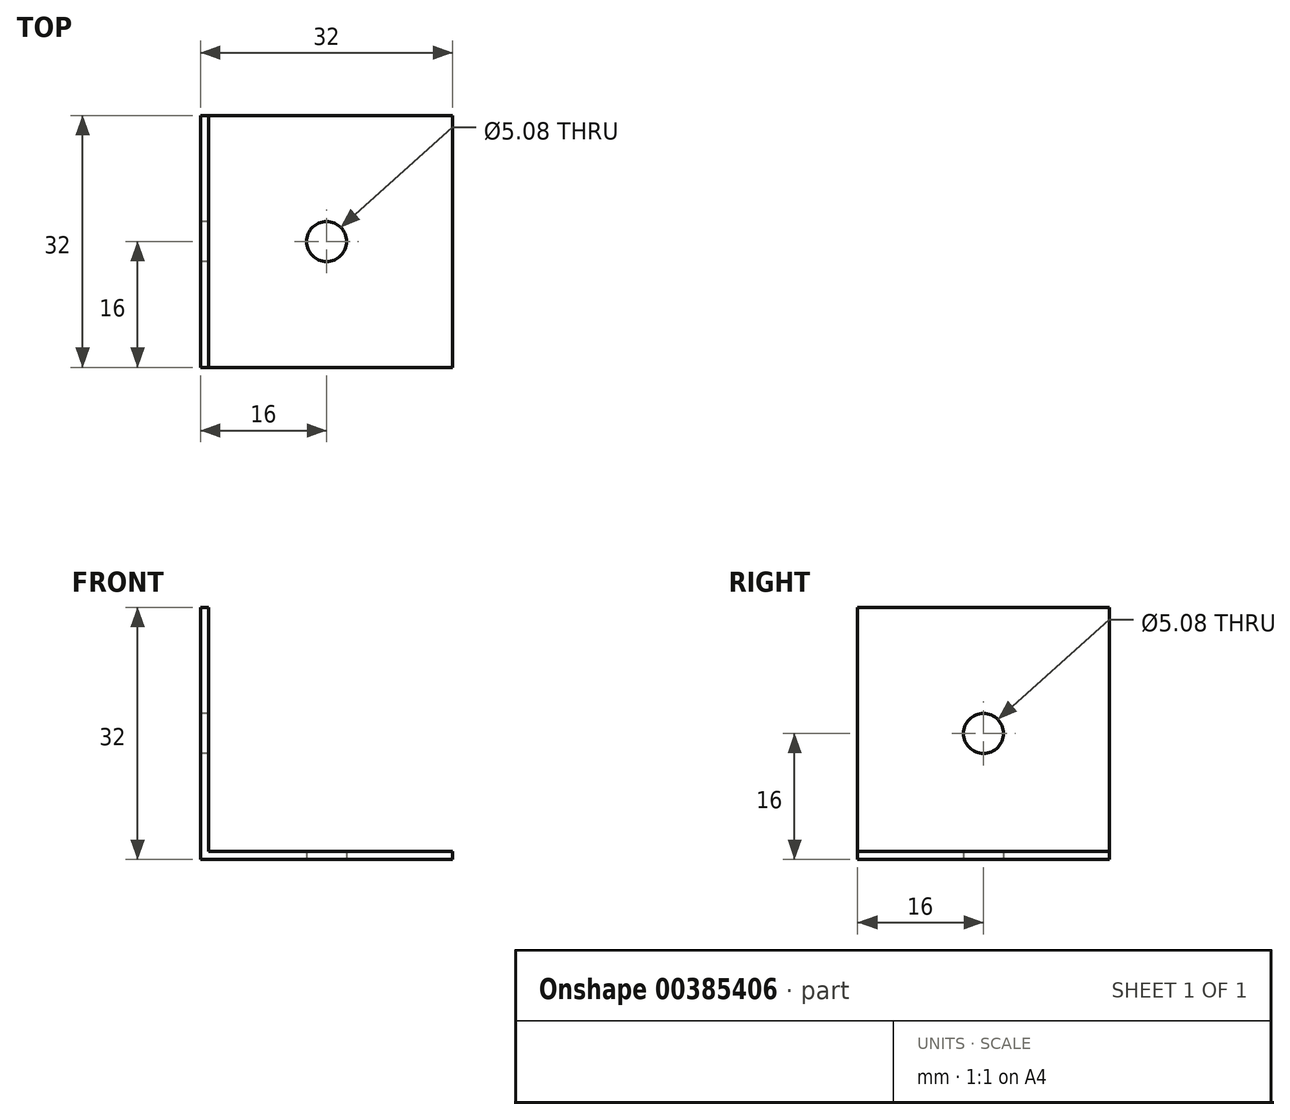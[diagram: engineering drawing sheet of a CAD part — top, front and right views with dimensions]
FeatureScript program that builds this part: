
annotation { "Feature Type Name" : "Feature", "Feature Type Description" : "" }
export const myFeature = defineFeature(function(context is Context, id is Id, definition is map)
    precondition{}
    {
        {
            var Q0;
            Q0=qCreatedBy(makeId("Front.planeOp"),FACE);
            var sketch = newSketch(context, id + "F0", { "sketchPlane" : qUnion([Q0])});
            skLineSegment(sketch, "E0", {"start": v(-16, 15.75) * mm, "end": v(-16, -16.25) * mm});
            skLineSegment(sketch, "E1", {"start": v(-16, -16.25) * mm, "end": v(16, -16.25) * mm});
            skLineSegment(sketch, "E2", {"start": v(16, -16.25) * mm, "end": v(16, -15.25) * mm});
            skLineSegment(sketch, "E3", {"start": v(16, -15.25) * mm, "end": v(-15, -15.25) * mm});
            skLineSegment(sketch, "E4", {"start": v(-15, -15.25) * mm, "end": v(-15, 15.75) * mm});
            skLineSegment(sketch, "E5", {"start": v(-15, 15.75) * mm, "end": v(-16, 15.75) * mm});
            skSolve(sketch);
        }
        {
            var Q0;
            Q0=qSketchRegion(id+"F0",true);
            extrude(context, id + "F1", {"entities" : qUnion([Q0]), "depth" : 32 * mm});
        }
        {
            var Q0;
            Q0=makeQuery(id+"F1.opExtrude","SWEPT_FACE",FACE,{"disambiguationData":[OSD([sQuery(id+"F0.wireOp",EDGE,"E0")])]});
            var sketch = newSketch(context, id + "F2", { "sketchPlane" : qUnion([Q0])});
            skPoint(sketch, "E6", {"position": v(16, -0.25) * mm});
            skCircle(sketch, "E7", {"center": v(16, -0.25) * mm, "radius": 2.54 * mm});
            skSolve(sketch);
        }
        {
            var Q0;
            Q0=qSketchRegion(id+"F2",true);
            extrude(context, id + "F3", {"entities" : qUnion([Q0]), "operationType" : NewBodyOperationType.REMOVE, "oppositeDirection" : true, "depth" : 25.4 * mm});
        }
        {
            var Q0;
            Q0=makeQuery(id+"F1.opExtrude","SWEPT_FACE",FACE,{"disambiguationData":[OSD([sQuery(id+"F0.wireOp",EDGE,"E1")])]});
            var sketch = newSketch(context, id + "F4", { "sketchPlane" : qUnion([Q0])});
            skPoint(sketch, "E8", {"position": v(0, 16) * mm});
            skCircle(sketch, "E9", {"center": v(0, 16) * mm, "radius": 2.54 * mm});
            skSolve(sketch);
        }
        {
            var Q0;
            Q0=qSketchRegion(id+"F4",true);
            extrude(context, id + "F5", {"entities" : qUnion([Q0]), "operationType" : NewBodyOperationType.REMOVE, "oppositeDirection" : true, "depth" : 25.4 * mm});
        }
    });
